# Revit family: C Series - C920STIO - Front Intake
name_source: partatom
category: Generic Models
units: mm (PartAtom-declared; Revit-internal decimal feet)

## family parameters
Can host rebar = No
Cut with Voids When Loaded = Yes
Host = Face
Part Type = Normal
Room Calculation Point = No
Round Connector Dimension = Use Diameter
Shared = Yes

## types (1)
- As Specified
    Assembly Code = D3020
    Base Height = 15"
    Base Offset = 1"
    Base Offset Left = 9"
    Base Offset Right = 9"
    COOLPack Consumption = 1200 CFM
    Default Elevation = 48"
    Depth = 20 7/8"
    Description = Montigo Fireplace as Specified
    Fire Place Opening = 29"
    Fire Place Opening Length = 43"
    Firebox Material = Metal - Montigo - White
    Frame Material = Metal - Montigo - Black
    Glazing Tint = Glass - Montigo - Tint as Specified
    HVAC_BTU Input = 0.0 Btu/h
    HVAC_BTU Output = 0.0 Btu/h
    HVAC_Entry Diameter = 7"
    HVAC_Exit Diameter = 8"
    Height = 51 7/16"
    Intake Duct Offset = 6"
    Length = 120 3/16"
    Manufacturer = Montigo
    Manufacturer Website = https://www.montigo.com
    Top Offset Left = 0"
    Top Offset Right = 0"
    URL = https://www.montigo.com

## geometry (parser evidence)
native form markers: Blend x2, Sweep x6
no freeform markers — native parametric forms only
